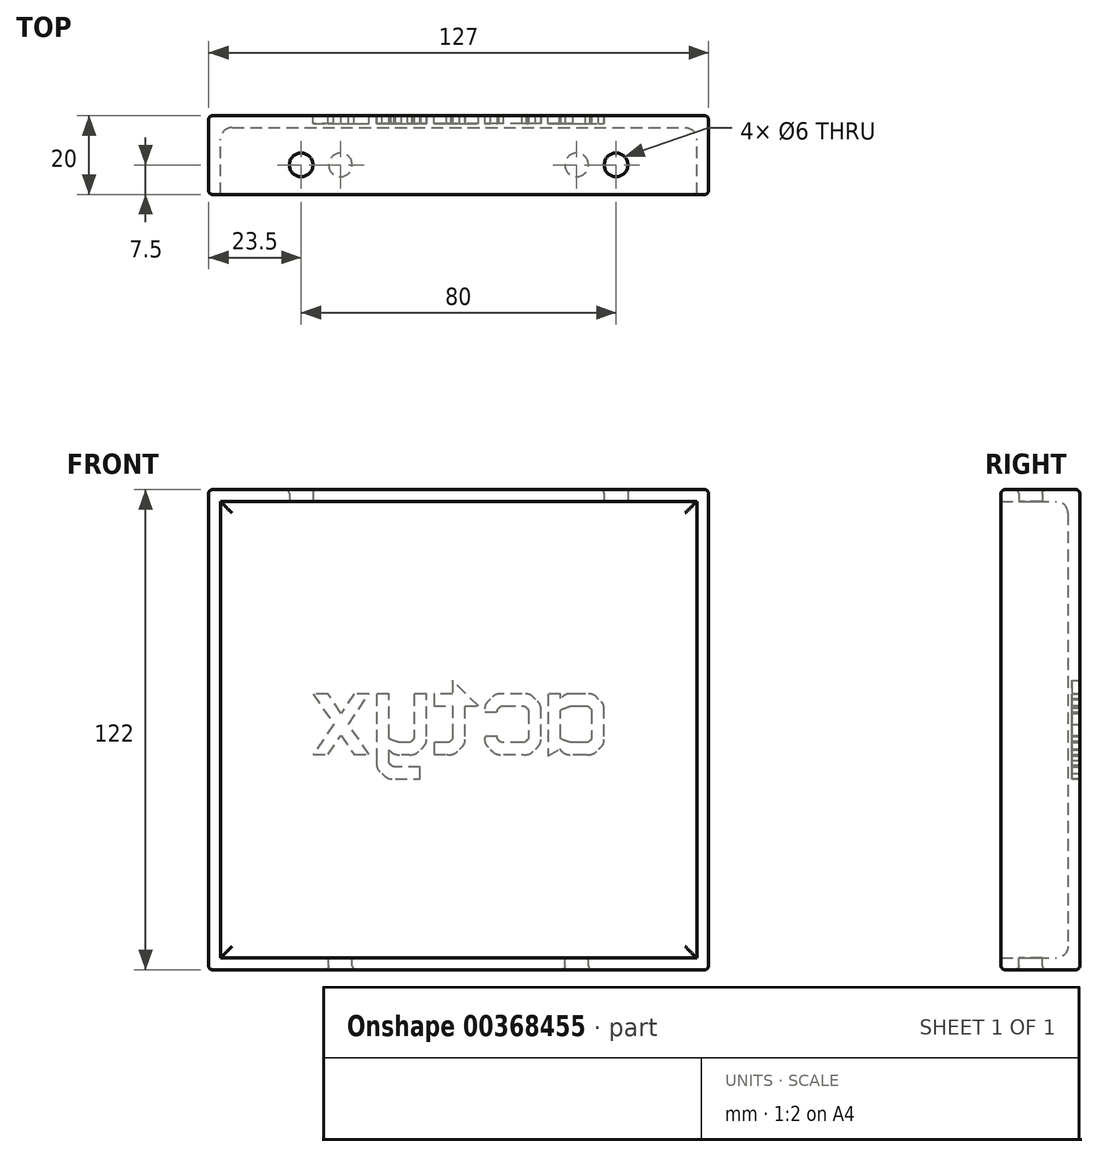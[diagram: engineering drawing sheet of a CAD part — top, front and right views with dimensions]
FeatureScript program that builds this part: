
annotation { "Feature Type Name" : "Feature", "Feature Type Description" : "" }
export const myFeature = defineFeature(function(context is Context, id is Id, definition is map)
    precondition{}
    {
        {
            var Q0;
            Q0=qCreatedBy(makeId("Front.planeOp"),FACE);
            var sketch = newSketch(context, id + "F0", { "sketchPlane" : qUnion([Q0])});
            skLineSegment(sketch, "E0.bottom", {"start": v(-63.5, 61) * mm, "end": v(63.5, 61) * mm});
            skLineSegment(sketch, "E0.top", {"start": v(-63.5, -61) * mm, "end": v(63.5, -61) * mm});
            skLineSegment(sketch, "E0.left", {"start": v(-63.5, 61) * mm, "end": v(-63.5, -61) * mm});
            skLineSegment(sketch, "E0.right", {"start": v(63.5, 61) * mm, "end": v(63.5, -61) * mm});
            skSolve(sketch);
        }
        {
            var Q0;
            Q0 = qSketchRegion(id + "F0", true);
            extrude(context, id + "F1", {"entities" : qUnion([Q0]), "depth" : 20 * mm});
        }
        {
            var Q0;
            Q0=makeQuery(id+"F1.opExtrude","CAP_FACE",FACE,{"disambiguationData":[OSD([sQuery(id+"F0.wireOp",EDGE,"E0.bottom"),sQuery(id+"F0.wireOp",EDGE,"E0.top"),sQuery(id+"F0.wireOp",EDGE,"E0.left"),sQuery(id+"F0.wireOp",EDGE,"E0.right")])],"isStart":false});
            shell(context, id + "F2", {"entities" : qUnion([Q0]), "thickness" : 3 * mm});
        }
        {
            var Q0;
            Q0=makeQuery(id+"F2.opShell","OFFSET_FACE",FACE,{"disambiguationData":[OSD([sQuery(id+"F0.wireOp",EDGE,"E0.bottom")])]});
            var sketch = newSketch(context, id + "F3", { "sketchPlane" : qUnion([Q0])});
            skPoint(sketch, "E1", {"position": v(-40, 12.5) * mm});
            skPoint(sketch, "E2.MirrorP", {"position": v(40, 12.5) * mm});
            skSolve(sketch);
        }
        {
            var Q0;
            Q0=sQuery(id+"F3.wireOp",VERTEX,"E1");
            var Q1;
            Q1=sQuery(id+"F3.wireOp",VERTEX,"E2.MirrorP");
            var Q2;
            Q2=makeQuery(id+"F1.opExtrude","SWEPT_BODY",BODY,{"disambiguationData":[OSD([sQuery(id+"F0.wireOp",EDGE,"E0.bottom"),sQuery(id+"F0.wireOp",EDGE,"E0.top"),sQuery(id+"F0.wireOp",EDGE,"E0.left"),sQuery(id+"F0.wireOp",EDGE,"E0.right")])]});
            hole(context, id + "F4", {"style" : HoleStyle.SIMPLE, "endStyle" : HoleEndStyle.THROUGH, "holeDiameter" : 6 * mm, "isTappedThrough" : true, "tappedDepth" : 12 * mm, "tapClearance" : 3, "locations" : qUnion([Q0, Q1]), "scope" : qUnion([Q2])});
        }
        {
            var Q0;
            Q0=makeQuery(id+"F2.opShell","OFFSET_FACE",FACE,{"disambiguationData":[OSD([sQuery(id+"F0.wireOp",EDGE,"E0.top")])]});
            var sketch = newSketch(context, id + "F5", { "sketchPlane" : qUnion([Q0])});
            skPoint(sketch, "E3", {"position": v(-30, -12.5) * mm});
            skPoint(sketch, "E4.MirrorP", {"position": v(30, -12.5) * mm});
            skSolve(sketch);
        }
        {
            var Q0;
            Q0=sQuery(id+"F5.wireOp",VERTEX,"E3");
            var Q1;
            Q1=sQuery(id+"F5.wireOp",VERTEX,"E4.MirrorP");
            var Q2;
            Q2=makeQuery(id+"F1.opExtrude","SWEPT_BODY",BODY,{"disambiguationData":[OSD([sQuery(id+"F0.wireOp",EDGE,"E0.bottom"),sQuery(id+"F0.wireOp",EDGE,"E0.top"),sQuery(id+"F0.wireOp",EDGE,"E0.left"),sQuery(id+"F0.wireOp",EDGE,"E0.right")])]});
            hole(context, id + "F6", {"style" : HoleStyle.SIMPLE, "endStyle" : HoleEndStyle.THROUGH, "holeDiameter" : 6 * mm, "isTappedThrough" : true, "tappedDepth" : 12 * mm, "tapClearance" : 3, "locations" : qUnion([Q0, Q1]), "scope" : qUnion([Q2])});
        }
        {
            var Q0;
            Q0=makeQuery(id+"F2.opShell","OFFSET_FACE",FACE,{"disambiguationData":[OSD([sQuery(id+"F0.wireOp",EDGE,"E0.bottom"),sQuery(id+"F0.wireOp",EDGE,"E0.top"),sQuery(id+"F0.wireOp",EDGE,"E0.left"),sQuery(id+"F0.wireOp",EDGE,"E0.right")])]});
            fillet(context, id + "F7", {"entities" : qUnion([Q0]), "radius" : 3 * mm, "tangentPropagation" : true, "allowEdgeOverflow" : false});
        }
        {
            var Q0;
            Q0=makeQuery(id+"F1.opExtrude","CAP_FACE",FACE,{"disambiguationData":[OSD([sQuery(id+"F0.wireOp",EDGE,"E0.bottom"),sQuery(id+"F0.wireOp",EDGE,"E0.top"),sQuery(id+"F0.wireOp",EDGE,"E0.left"),sQuery(id+"F0.wireOp",EDGE,"E0.right")])],"isStart":true});
            var sketch = newSketch(context, id + "F8", { "sketchPlane" : qUnion([Q0])});
            skLineSegment(sketch, "E5", {"start": v(-36.96, -1.7) * mm, "end": v(-36.96, 4.47) * mm});
            skFitSpline(sketch, "E6", {"points": [v(-36.96, 4.47) * mm, v(-36.96, 5.74) * mm, v(-36.5, 6.83) * mm, v(-35.57, 7.74) * mm]});
            skFitSpline(sketch, "E7", {"points": [v(-35.57, 7.74) * mm, v(-34.64, 8.64) * mm, v(-33.53, 9.1) * mm, v(-32.23, 9.1) * mm]});
            skLineSegment(sketch, "E8", {"start": v(-32.23, 9.1) * mm, "end": v(-29.07, 9.1) * mm});
            skFitSpline(sketch, "E9", {"points": [v(-29.07, 9.1) * mm, v(-27.85, 9.1) * mm, v(-26.8, 8.7) * mm, v(-25.92, 7.9) * mm]});
            skLineSegment(sketch, "E10", {"start": v(-25.92, 7.9) * mm, "end": v(-25.92, 9.1) * mm});
            skLineSegment(sketch, "E11", {"start": v(-25.92, 9.1) * mm, "end": v(-22.77, 9.1) * mm});
            skLineSegment(sketch, "E12", {"start": v(-22.77, 9.1) * mm, "end": v(-22.77, -6.63) * mm});
            skLineSegment(sketch, "E13", {"start": v(-22.77, -6.63) * mm, "end": v(-25.68, -4.92) * mm});
            skFitSpline(sketch, "E14", {"points": [v(-25.68, -4.92) * mm, v(-25.7, -4.94) * mm, v(-25.72, -4.95) * mm, v(-25.73, -4.96) * mm]});
            skFitSpline(sketch, "E15", {"points": [v(-25.73, -4.96) * mm, v(-26.65, -5.87) * mm, v(-27.77, -6.32) * mm, v(-29.07, -6.32) * mm]});
            skLineSegment(sketch, "E16", {"start": v(-29.07, -6.32) * mm, "end": v(-32.23, -6.32) * mm});
            skFitSpline(sketch, "E17", {"points": [v(-32.23, -6.32) * mm, v(-33.53, -6.32) * mm, v(-34.64, -5.87) * mm, v(-35.57, -4.96) * mm]});
            skFitSpline(sketch, "E18", {"points": [v(-35.57, -4.96) * mm, v(-36.5, -4.06) * mm, v(-36.96, -2.97) * mm, v(-36.96, -1.7) * mm]});
            skLineSegment(sketch, "E19", {"start": v(-33.8, 4.47) * mm, "end": v(-33.8, -1.7) * mm});
            skFitSpline(sketch, "E20", {"points": [v(-33.8, -1.7) * mm, v(-33.8, -2.12) * mm, v(-33.65, -2.48) * mm, v(-33.34, -2.79) * mm]});
            skFitSpline(sketch, "E21", {"points": [v(-33.34, -2.79) * mm, v(-33.03, -3.09) * mm, v(-32.66, -3.24) * mm, v(-32.23, -3.24) * mm]});
            skLineSegment(sketch, "E22", {"start": v(-32.23, -3.24) * mm, "end": v(-29.07, -3.24) * mm});
            skFitSpline(sketch, "E23", {"points": [v(-29.07, -3.24) * mm, v(-28.64, -3.24) * mm, v(-28.01, -3.09) * mm, v(-27.18, -2.79) * mm]});
            skFitSpline(sketch, "E24", {"points": [v(-27.18, -2.79) * mm, v(-26.34, -2.48) * mm, v(-25.92, -2.12) * mm, v(-25.92, -1.7) * mm]});
            skLineSegment(sketch, "E25", {"start": v(-25.92, -1.7) * mm, "end": v(-25.92, 4.47) * mm});
            skFitSpline(sketch, "E26", {"points": [v(-25.92, 4.47) * mm, v(-25.92, 4.9) * mm, v(-26.34, 5.25) * mm, v(-27.18, 5.55) * mm]});
            skFitSpline(sketch, "E27", {"points": [v(-27.18, 5.55) * mm, v(-28.01, 5.86) * mm, v(-28.64, 6.01) * mm, v(-29.07, 6.01) * mm]});
            skLineSegment(sketch, "E28", {"start": v(-29.07, 6.01) * mm, "end": v(-32.23, 6.01) * mm});
            skFitSpline(sketch, "E29", {"points": [v(-32.23, 6.01) * mm, v(-32.66, 6.01) * mm, v(-33.03, 5.86) * mm, v(-33.34, 5.55) * mm]});
            skFitSpline(sketch, "E30", {"points": [v(-33.34, 5.55) * mm, v(-33.65, 5.25) * mm, v(-33.8, 4.9) * mm, v(-33.8, 4.47) * mm]});
            skFitSpline(sketch, "E31", {"points": [v(-11.41, 9.1) * mm, v(-10.11, 9.1) * mm, v(-9, 8.64) * mm, v(-8.07, 7.74) * mm]});
            skFitSpline(sketch, "E32", {"points": [v(-8.07, 7.74) * mm, v(-7.15, 6.83) * mm, v(-6.68, 5.74) * mm, v(-6.68, 4.47) * mm]});
            skLineSegment(sketch, "E33", {"start": v(-6.68, 4.47) * mm, "end": v(-9.84, 4.47) * mm});
            skFitSpline(sketch, "E34", {"points": [v(-9.84, 4.47) * mm, v(-9.84, 4.9) * mm, v(-10, 5.25) * mm, v(-10.31, 5.55) * mm]});
            skFitSpline(sketch, "E35", {"points": [v(-10.31, 5.55) * mm, v(-10.62, 5.86) * mm, v(-10.98, 6.01) * mm, v(-11.41, 6.01) * mm]});
            skLineSegment(sketch, "E36", {"start": v(-11.41, 6.01) * mm, "end": v(-16.14, 6.01) * mm});
            skFitSpline(sketch, "E37", {"points": [v(-16.14, 6.01) * mm, v(-16.58, 6.01) * mm, v(-16.95, 5.86) * mm, v(-17.26, 5.55) * mm]});
            skFitSpline(sketch, "E38", {"points": [v(-17.26, 5.55) * mm, v(-17.57, 5.25) * mm, v(-17.72, 4.9) * mm, v(-17.72, 4.47) * mm]});
            skLineSegment(sketch, "E39", {"start": v(-17.72, 4.47) * mm, "end": v(-17.72, -1.7) * mm});
            skFitSpline(sketch, "E40", {"points": [v(-17.72, -1.7) * mm, v(-17.72, -2.12) * mm, v(-17.57, -2.48) * mm, v(-17.26, -2.79) * mm]});
            skFitSpline(sketch, "E41", {"points": [v(-17.26, -2.79) * mm, v(-16.95, -3.09) * mm, v(-16.58, -3.24) * mm, v(-16.14, -3.24) * mm]});
            skLineSegment(sketch, "E42", {"start": v(-16.14, -3.24) * mm, "end": v(-11.41, -3.24) * mm});
            skFitSpline(sketch, "E43", {"points": [v(-11.41, -3.24) * mm, v(-10.98, -3.24) * mm, v(-10.62, -3.09) * mm, v(-10.31, -2.79) * mm]});
            skFitSpline(sketch, "E44", {"points": [v(-10.31, -2.79) * mm, v(-10, -2.48) * mm, v(-9.84, -2.12) * mm, v(-9.84, -1.7) * mm]});
            skLineSegment(sketch, "E45", {"start": v(-9.84, -1.7) * mm, "end": v(-6.68, -1.7) * mm});
            skFitSpline(sketch, "E46", {"points": [v(-6.68, -1.7) * mm, v(-6.68, -2.97) * mm, v(-7.15, -4.06) * mm, v(-8.07, -4.96) * mm]});
            skFitSpline(sketch, "E47", {"points": [v(-8.07, -4.96) * mm, v(-9, -5.87) * mm, v(-10.11, -6.32) * mm, v(-11.41, -6.32) * mm]});
            skLineSegment(sketch, "E48", {"start": v(-11.41, -6.32) * mm, "end": v(-16.14, -6.32) * mm});
            skFitSpline(sketch, "E49", {"points": [v(-16.14, -6.32) * mm, v(-17.45, -6.32) * mm, v(-18.56, -5.87) * mm, v(-19.49, -4.96) * mm]});
            skFitSpline(sketch, "E50", {"points": [v(-19.49, -4.96) * mm, v(-20.41, -4.06) * mm, v(-20.87, -2.97) * mm, v(-20.87, -1.7) * mm]});
            skLineSegment(sketch, "E51", {"start": v(-20.87, -1.7) * mm, "end": v(-20.87, 4.47) * mm});
            skFitSpline(sketch, "E52", {"points": [v(-20.87, 4.47) * mm, v(-20.87, 5.74) * mm, v(-20.41, 6.83) * mm, v(-19.49, 7.74) * mm]});
            skFitSpline(sketch, "E53", {"points": [v(-19.49, 7.74) * mm, v(-18.56, 8.64) * mm, v(-17.45, 9.1) * mm, v(-16.14, 9.1) * mm]});
            skLineSegment(sketch, "E54", {"start": v(-16.14, 9.1) * mm, "end": v(-11.41, 9.1) * mm});
            skLineSegment(sketch, "E55", {"start": v(3.1, -3.24) * mm, "end": v(6.26, -3.24) * mm});
            skLineSegment(sketch, "E56", {"start": v(6.26, -3.24) * mm, "end": v(6.26, -6.32) * mm});
            skLineSegment(sketch, "E57", {"start": v(6.26, -6.32) * mm, "end": v(3.1, -6.32) * mm});
            skFitSpline(sketch, "E58", {"points": [v(3.1, -6.32) * mm, v(1.8, -6.32) * mm, v(0.69, -5.87) * mm, v(-0.24, -4.96) * mm]});
            skFitSpline(sketch, "E59", {"points": [v(-0.24, -4.96) * mm, v(-1.16, -4.06) * mm, v(-1.62, -2.97) * mm, v(-1.62, -1.7) * mm]});
            skLineSegment(sketch, "E60", {"start": v(-1.62, -1.7) * mm, "end": v(-1.62, 6.01) * mm});
            skLineSegment(sketch, "E61", {"start": v(-1.62, 6.01) * mm, "end": v(-5.1, 6.01) * mm});
            skLineSegment(sketch, "E62", {"start": v(-5.1, 6.01) * mm, "end": v(1.53, 12.49) * mm});
            skLineSegment(sketch, "E63", {"start": v(1.53, 12.49) * mm, "end": v(1.53, 9.1) * mm});
            skLineSegment(sketch, "E64", {"start": v(1.53, 9.1) * mm, "end": v(6.26, 9.1) * mm});
            skLineSegment(sketch, "E65", {"start": v(6.26, 9.1) * mm, "end": v(6.26, 6.01) * mm});
            skLineSegment(sketch, "E66", {"start": v(6.26, 6.01) * mm, "end": v(1.53, 6.01) * mm});
            skLineSegment(sketch, "E67", {"start": v(1.53, 6.01) * mm, "end": v(1.53, -1.7) * mm});
            skFitSpline(sketch, "E68", {"points": [v(1.53, -1.7) * mm, v(1.53, -2.12) * mm, v(1.68, -2.48) * mm, v(1.99, -2.79) * mm]});
            skFitSpline(sketch, "E69", {"points": [v(1.99, -2.79) * mm, v(2.3, -3.09) * mm, v(2.67, -3.24) * mm, v(3.1, -3.24) * mm]});
            skLineSegment(sketch, "E70", {"start": v(8.2, -1.7) * mm, "end": v(8.2, 9.1) * mm});
            skLineSegment(sketch, "E71", {"start": v(8.2, 9.1) * mm, "end": v(11.35, 9.1) * mm});
            skLineSegment(sketch, "E72", {"start": v(11.35, 9.1) * mm, "end": v(11.35, -1.7) * mm});
            skFitSpline(sketch, "E73", {"points": [v(11.35, -1.7) * mm, v(11.35, -2.12) * mm, v(11.5, -2.48) * mm, v(11.8, -2.79) * mm]});
            skFitSpline(sketch, "E74", {"points": [v(11.8, -2.79) * mm, v(12.12, -3.09) * mm, v(12.5, -3.24) * mm, v(12.93, -3.24) * mm]});
            skLineSegment(sketch, "E75", {"start": v(12.93, -3.24) * mm, "end": v(14.5, -3.24) * mm});
            skFitSpline(sketch, "E76", {"points": [v(14.5, -3.24) * mm, v(14.94, -3.24) * mm, v(15.57, -3.09) * mm, v(16.4, -2.79) * mm]});
            skFitSpline(sketch, "E77", {"points": [v(16.4, -2.79) * mm, v(17.24, -2.48) * mm, v(17.66, -2.12) * mm, v(17.66, -1.7) * mm]});
            skLineSegment(sketch, "E78", {"start": v(17.66, -1.7) * mm, "end": v(17.66, 9.1) * mm});
            skLineSegment(sketch, "E79", {"start": v(17.66, 9.1) * mm, "end": v(20.81, 9.1) * mm});
            skLineSegment(sketch, "E80", {"start": v(20.81, 9.1) * mm, "end": v(20.81, -7.86) * mm});
            skFitSpline(sketch, "E81", {"points": [v(20.81, -7.86) * mm, v(20.81, -9.14) * mm, v(20.35, -10.22) * mm, v(19.42, -11.13) * mm]});
            skFitSpline(sketch, "E82", {"points": [v(19.42, -11.13) * mm, v(18.5, -12.03) * mm, v(17.38, -12.49) * mm, v(16.08, -12.49) * mm]});
            skLineSegment(sketch, "E83", {"start": v(16.08, -12.49) * mm, "end": v(9.77, -12.49) * mm});
            skLineSegment(sketch, "E84", {"start": v(9.77, -12.49) * mm, "end": v(9.77, -9.4) * mm});
            skLineSegment(sketch, "E85", {"start": v(9.77, -9.4) * mm, "end": v(16.08, -9.4) * mm});
            skFitSpline(sketch, "E86", {"points": [v(16.08, -9.4) * mm, v(16.51, -9.4) * mm, v(16.88, -9.25) * mm, v(17.18, -8.94) * mm]});
            skFitSpline(sketch, "E87", {"points": [v(17.18, -8.94) * mm, v(17.5, -8.64) * mm, v(17.66, -8.28) * mm, v(17.66, -7.86) * mm]});
            skLineSegment(sketch, "E88", {"start": v(17.66, -7.86) * mm, "end": v(17.66, -5.13) * mm});
            skFitSpline(sketch, "E89", {"points": [v(17.66, -5.13) * mm, v(16.77, -5.92) * mm, v(15.72, -6.32) * mm, v(14.5, -6.32) * mm]});
            skLineSegment(sketch, "E90", {"start": v(14.5, -6.32) * mm, "end": v(12.93, -6.32) * mm});
            skFitSpline(sketch, "E91", {"points": [v(12.93, -6.32) * mm, v(11.62, -6.32) * mm, v(10.51, -5.87) * mm, v(9.59, -4.96) * mm]});
            skFitSpline(sketch, "E92", {"points": [v(9.59, -4.96) * mm, v(8.66, -4.06) * mm, v(8.2, -2.97) * mm, v(8.2, -1.7) * mm]});
            skLineSegment(sketch, "E93", {"start": v(27.97, 1.39) * mm, "end": v(22.77, 9.1) * mm});
            skLineSegment(sketch, "E94", {"start": v(22.77, 9.1) * mm, "end": v(26.55, 9.1) * mm});
            skLineSegment(sketch, "E95", {"start": v(26.55, 9.1) * mm, "end": v(29.86, 4.2) * mm});
            skLineSegment(sketch, "E96", {"start": v(29.86, 4.2) * mm, "end": v(33.17, 9.1) * mm});
            skLineSegment(sketch, "E97", {"start": v(33.17, 9.1) * mm, "end": v(36.96, 9.1) * mm});
            skLineSegment(sketch, "E98", {"start": v(36.96, 9.1) * mm, "end": v(31.75, 1.39) * mm});
            skLineSegment(sketch, "E99", {"start": v(31.75, 1.39) * mm, "end": v(36.96, -6.32) * mm});
            skLineSegment(sketch, "E100", {"start": v(36.96, -6.32) * mm, "end": v(33.17, -6.32) * mm});
            skLineSegment(sketch, "E101", {"start": v(33.17, -6.32) * mm, "end": v(29.86, -1.42) * mm});
            skLineSegment(sketch, "E102", {"start": v(29.86, -1.42) * mm, "end": v(26.55, -6.32) * mm});
            skLineSegment(sketch, "E103", {"start": v(26.55, -6.32) * mm, "end": v(22.77, -6.32) * mm});
            skLineSegment(sketch, "E104", {"start": v(22.77, -6.32) * mm, "end": v(27.97, 1.39) * mm});
            skSolve(sketch);
        }
        {
            var Q0;
            Q0 = qSketchRegion(id + "F8", true);
            extrude(context, id + "F9", {"entities" : qUnion([Q0]), "operationType" : NewBodyOperationType.REMOVE, "oppositeDirection" : true, "depth" : 2 * mm});
        }
        {
            var Q0;
            Q0=makeQuery(id+"F1.opExtrude","SWEPT_FACE",FACE,{"disambiguationData":[OSD([sQuery(id+"F0.wireOp",EDGE,"E0.right")])]});
            var Q1;
            Q1=makeQuery(id+"F1.opExtrude","SWEPT_FACE",FACE,{"disambiguationData":[OSD([sQuery(id+"F0.wireOp",EDGE,"E0.bottom")])]});
            var Q2;
            Q2=makeQuery(id+"F1.opExtrude","SWEPT_FACE",FACE,{"disambiguationData":[OSD([sQuery(id+"F0.wireOp",EDGE,"E0.left")])]});
            var Q3;
            Q3=makeQuery(id+"F1.opExtrude","SWEPT_FACE",FACE,{"disambiguationData":[OSD([sQuery(id+"F0.wireOp",EDGE,"E0.top")])]});
            fillet(context, id + "F10", {"entities" : qUnion([Q0, Q1, Q2, Q3]), "radius" : 1 * mm, "tangentPropagation" : true, "allowEdgeOverflow" : false});
        }
    });
